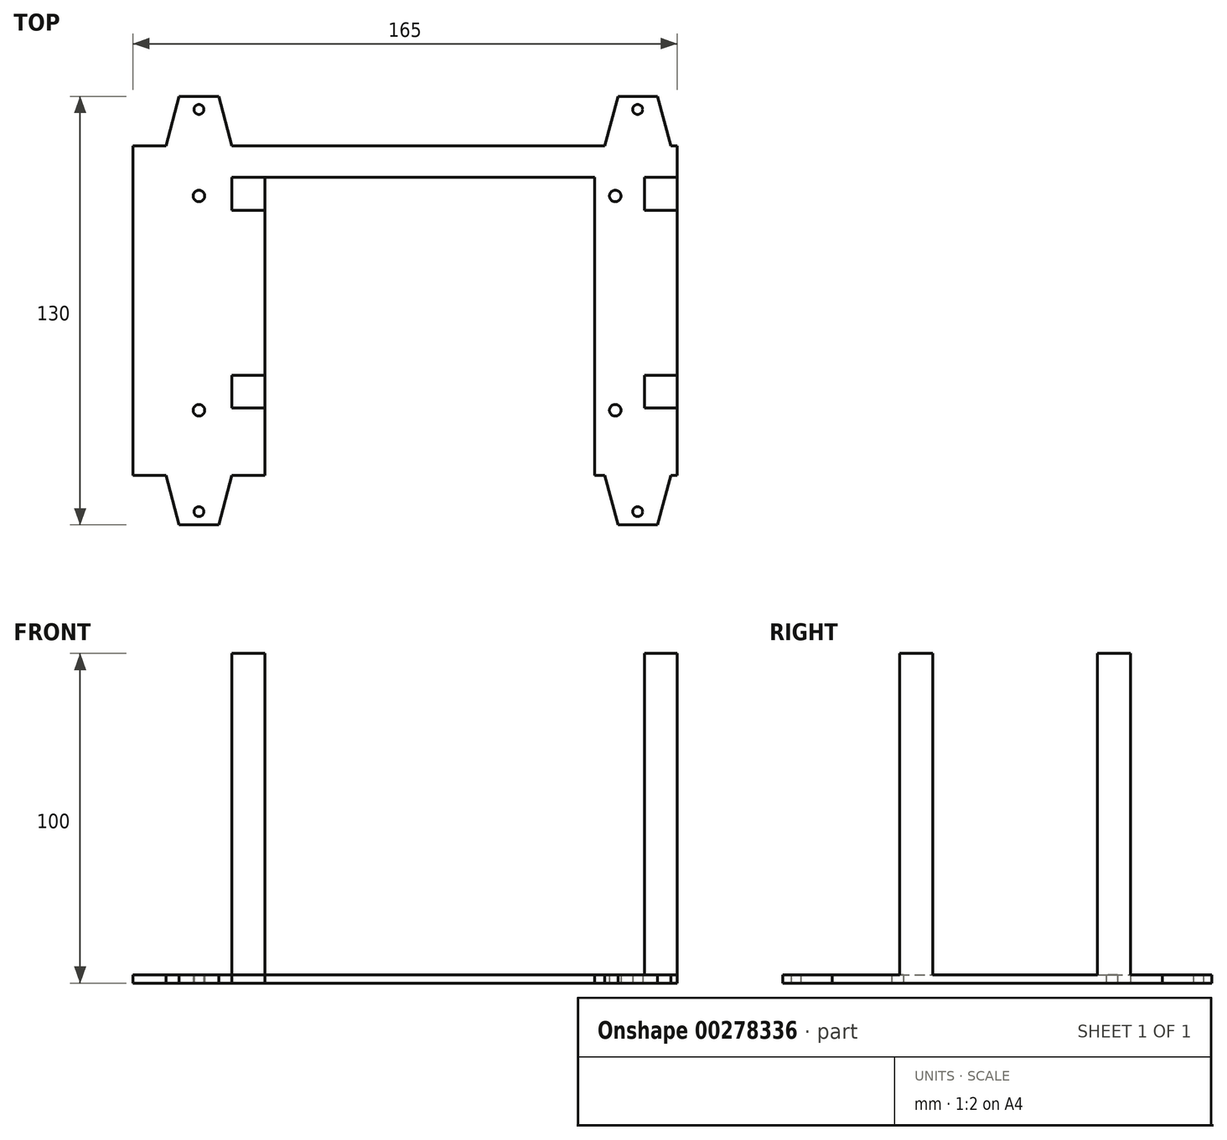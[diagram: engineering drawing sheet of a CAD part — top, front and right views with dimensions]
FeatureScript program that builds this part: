
annotation { "Feature Type Name" : "Feature", "Feature Type Description" : "" }
export const myFeature = defineFeature(function(context is Context, id is Id, definition is map)
    precondition{}
    {
        {
            var Q0;
            Q0=qCreatedBy(makeId("Top.planeOp"),FACE);
            var sketch = newSketch(context, id + "F0", { "sketchPlane" : qUnion([Q0])});
            skLineSegment(sketch, "E0.bottom", {"start": v(-57.92, 32.15) * mm, "end": v(107.08, 32.15) * mm});
            skLineSegment(sketch, "E0.top", {"start": v(-57.92, -67.85) * mm, "end": v(107.08, -67.85) * mm});
            skLineSegment(sketch, "E0.left", {"start": v(-57.92, 32.15) * mm, "end": v(-57.92, -67.85) * mm});
            skLineSegment(sketch, "E0.right", {"start": v(107.08, 32.15) * mm, "end": v(107.08, -67.85) * mm});
            skLineSegment(sketch, "E1.bottom", {"start": v(-17.92, 12.54) * mm, "end": v(82.08, 12.54) * mm});
            skLineSegment(sketch, "E1.top", {"start": v(-17.92, -67.85) * mm, "end": v(82.08, -67.85) * mm});
            skLineSegment(sketch, "E1.left", {"start": v(-17.92, 12.54) * mm, "end": v(-17.92, -67.85) * mm});
            skLineSegment(sketch, "E1.right", {"start": v(82.08, 12.54) * mm, "end": v(82.08, -67.85) * mm});
            skCircle(sketch, "E2", {"center": v(-37.92, 16.9) * mm, "radius": 1.75 * mm});
            skCircle(sketch, "E3.0.1.0", {"center": v(-37.92, -48.1) * mm, "radius": 1.75 * mm});
            skCircle(sketch, "E3.1.0.0", {"center": v(88.28, 16.9) * mm, "radius": 1.75 * mm});
            skCircle(sketch, "E3.1.1.0", {"center": v(88.28, -48.1) * mm, "radius": 1.75 * mm});
            skLineSegment(sketch, "E3.direction1", {"start": v(-37.92, 16.9) * mm, "end": v(88.28, 16.9) * mm, "construction": true});
            skLineSegment(sketch, "E3.direction2", {"start": v(-37.92, 16.9) * mm, "end": v(-37.92, -48.1) * mm, "construction": true});
            skLineSegment(sketch, "E4", {"start": v(-47.92, 32.15) * mm, "end": v(-43.9, 47.15) * mm});
            skLineSegment(sketch, "E5", {"start": v(-43.9, 47.15) * mm, "end": v(-31.94, 47.15) * mm});
            skLineSegment(sketch, "E6", {"start": v(-31.94, 47.15) * mm, "end": v(-27.92, 32.15) * mm});
            skLineSegment(sketch, "E7.MirrorCS", {"start": v(-31.94, -82.85) * mm, "end": v(-27.92, -67.85) * mm});
            skLineSegment(sketch, "E8.MirrorCS", {"start": v(-43.9, -82.85) * mm, "end": v(-31.94, -82.85) * mm});
            skLineSegment(sketch, "E9.MirrorCS", {"start": v(-47.92, -67.85) * mm, "end": v(-43.9, -82.85) * mm});
            skLineSegment(sketch, "E10.1.0.0", {"start": v(89.1, 47.15) * mm, "end": v(101.06, 47.15) * mm});
            skLineSegment(sketch, "E10.1.0.1", {"start": v(85.08, 32.15) * mm, "end": v(89.1, 47.15) * mm});
            skLineSegment(sketch, "E10.1.0.2", {"start": v(101.06, 47.15) * mm, "end": v(105.08, 32.15) * mm});
            skLineSegment(sketch, "E10.1.0.3", {"start": v(85.08, -67.85) * mm, "end": v(89.1, -82.85) * mm});
            skLineSegment(sketch, "E10.1.0.4", {"start": v(101.06, -82.85) * mm, "end": v(105.08, -67.85) * mm});
            skLineSegment(sketch, "E10.1.0.5", {"start": v(89.1, -82.85) * mm, "end": v(101.06, -82.85) * mm});
            skLineSegment(sketch, "E10.direction1", {"start": v(-43.9, -82.85) * mm, "end": v(89.1, -82.85) * mm, "construction": true});
            skCircle(sketch, "E11", {"center": v(-37.92, 43.15) * mm, "radius": 1.5 * mm});
            skCircle(sketch, "E12.0.1.0", {"center": v(-37.92, -78.85) * mm, "radius": 1.5 * mm});
            skCircle(sketch, "E12.1.0.0", {"center": v(95.08, 43.15) * mm, "radius": 1.5 * mm});
            skCircle(sketch, "E12.1.1.0", {"center": v(95.08, -78.85) * mm, "radius": 1.5 * mm});
            skLineSegment(sketch, "E12.direction1", {"start": v(-37.92, 43.15) * mm, "end": v(95.08, 43.15) * mm, "construction": true});
            skLineSegment(sketch, "E12.direction2", {"start": v(-37.92, 43.15) * mm, "end": v(-37.92, -78.85) * mm, "construction": true});
            skLineSegment(sketch, "E13.bottom", {"start": v(-17.92, 12.54) * mm, "end": v(-27.92, 12.54) * mm});
            skLineSegment(sketch, "E13.top", {"start": v(-17.92, 22.54) * mm, "end": v(-27.92, 22.54) * mm});
            skLineSegment(sketch, "E13.left", {"start": v(-17.92, 12.54) * mm, "end": v(-17.92, 22.54) * mm});
            skLineSegment(sketch, "E13.right", {"start": v(-27.92, 12.54) * mm, "end": v(-27.92, 22.54) * mm});
            skLineSegment(sketch, "E14.0.1.0", {"start": v(-17.92, -47.46) * mm, "end": v(-27.92, -47.46) * mm});
            skLineSegment(sketch, "E14.0.1.1", {"start": v(-27.92, -47.46) * mm, "end": v(-27.92, -37.46) * mm});
            skLineSegment(sketch, "E14.0.1.2", {"start": v(-17.92, -37.46) * mm, "end": v(-27.92, -37.46) * mm});
            skLineSegment(sketch, "E14.0.1.3", {"start": v(-17.92, -47.46) * mm, "end": v(-17.92, -37.46) * mm});
            skLineSegment(sketch, "E14.1.0.0", {"start": v(107.08, 12.54) * mm, "end": v(97.08, 12.54) * mm});
            skLineSegment(sketch, "E14.1.0.1", {"start": v(97.08, 12.54) * mm, "end": v(97.08, 22.54) * mm});
            skLineSegment(sketch, "E14.1.0.2", {"start": v(107.08, 22.54) * mm, "end": v(97.08, 22.54) * mm});
            skLineSegment(sketch, "E14.1.0.3", {"start": v(107.08, 12.54) * mm, "end": v(107.08, 22.54) * mm});
            skLineSegment(sketch, "E14.1.1.0", {"start": v(107.08, -47.46) * mm, "end": v(97.08, -47.46) * mm});
            skLineSegment(sketch, "E14.1.1.1", {"start": v(97.08, -47.46) * mm, "end": v(97.08, -37.46) * mm});
            skLineSegment(sketch, "E14.1.1.2", {"start": v(107.08, -37.46) * mm, "end": v(97.08, -37.46) * mm});
            skLineSegment(sketch, "E14.1.1.3", {"start": v(107.08, -47.46) * mm, "end": v(107.08, -37.46) * mm});
            skLineSegment(sketch, "E14.direction1", {"start": v(-27.92, 12.54) * mm, "end": v(97.08, 12.54) * mm, "construction": true});
            skLineSegment(sketch, "E14.direction2", {"start": v(-27.92, 12.54) * mm, "end": v(-27.92, -47.46) * mm, "construction": true});
            skLineSegment(sketch, "E15", {"start": v(-17.92, 22.54) * mm, "end": v(97.08, 22.54) * mm});
            skLineSegment(sketch, "E16", {"start": v(82.08, 12.54) * mm, "end": v(82.08, 22.54) * mm});
            skSolve(sketch);
        }
        {
            var Q0;
            {var subQ6=sQuery(id+"F0.wireOp",EDGE,"E10.1.0.4");Q0=makeQuery(id+"F0.imprint","IMPRINT",FACE,{"disambiguationData":[TD([[makeQuery(id+"F0.imprint","IMPRINT",EDGE,{"derivedFrom":subQ6}),1.0]])]});}
            var Q1;
            {var subQ14=sQuery(id+"F0.wireOp",EDGE,"E0.left");Q1=makeQuery(id+"F0.imprint","IMPRINT",FACE,{"disambiguationData":[TD([[makeQuery(id+"F0.imprint","IMPRINT",EDGE,{"derivedFrom":subQ14}),1.0]])]});}
            var Q2;
            {var subQ1=sQuery(id+"F0.wireOp",EDGE,"E7.MirrorCS");Q2=makeQuery(id+"F0.imprint","IMPRINT",FACE,{"disambiguationData":[TD([[makeQuery(id+"F0.imprint","IMPRINT",EDGE,{"derivedFrom":subQ1}),1.0]])]});}
            var Q3;
            {var subQ1=sQuery(id+"F0.wireOp",EDGE,"E4");Q3=makeQuery(id+"F0.imprint","IMPRINT",FACE,{"disambiguationData":[TD([[makeQuery(id+"F0.imprint","IMPRINT",EDGE,{"derivedFrom":subQ1}),-1.0]])]});}
            var Q4;
            Q4=makeQuery(id+"F0.imprint","IMPRINT",FACE,{"disambiguationData":[TD([[makeQuery(id+"F0.imprint","IMPRINT",EDGE,{"derivedFrom":sQuery(id+"F0.wireOp",EDGE,"E10.1.0.0")}),-1.0]])]});
            var Q5;
            {var subQ1=sQuery(id+"F0.wireOp",EDGE,"E1.right");Q5=makeQuery(id+"F0.imprint","IMPRINT",FACE,{"disambiguationData":[TD([[makeQuery(id+"F0.imprint","IMPRINT",EDGE,{"derivedFrom":subQ1}),1.0]])]});}
            var Q6;
            {var subQ8=sQuery(id+"F0.wireOp",EDGE,"E10.1.0.3");Q6=makeQuery(id+"F0.imprint","IMPRINT",FACE,{"disambiguationData":[TD([[makeQuery(id+"F0.imprint","IMPRINT",EDGE,{"derivedFrom":subQ8}),1.0]])]});}
            extrude(context, id + "F1", {"entities" : qUnion([Q0, Q1, Q2, Q3, Q4, Q5, Q6]), "depth" : 2.5 * mm});
        }
        {
            var Q0;
            Q0=makeQuery(id+"F0.imprint","IMPRINT",FACE,{"disambiguationData":[TD([[makeQuery(id+"F0.imprint","IMPRINT",EDGE,{"derivedFrom":sQuery(id+"F0.wireOp",EDGE,"E13.bottom")}),-1.0]])]});
            var Q1;
            Q1=makeQuery(id+"F0.imprint","IMPRINT",FACE,{"disambiguationData":[TD([[makeQuery(id+"F0.imprint","IMPRINT",EDGE,{"derivedFrom":sQuery(id+"F0.wireOp",EDGE,"E14.1.0.0")}),-1.0]])]});
            var Q2;
            Q2=makeQuery(id+"F0.imprint","IMPRINT",FACE,{"disambiguationData":[TD([[makeQuery(id+"F0.imprint","IMPRINT",EDGE,{"derivedFrom":sQuery(id+"F0.wireOp",EDGE,"E14.1.1.0")}),-1.0]])]});
            var Q3;
            {var subQ0=sQuery(id+"F0.wireOp",EDGE,"E14.1.2.2");Q3=makeQuery(id+"F0.imprint","IMPRINT",FACE,{"disambiguationData":[TD([[makeQuery(id+"F0.imprint","IMPRINT",EDGE,{"derivedFrom":subQ0}),1.0]])]});}
            var Q4;
            Q4=makeQuery(id+"F0.imprint","IMPRINT",FACE,{"disambiguationData":[TD([[makeQuery(id+"F0.imprint","IMPRINT",EDGE,{"derivedFrom":sQuery(id+"F0.wireOp",EDGE,"E14.0.1.0")}),-1.0]])]});
            var Q5;
            {var subQ5=sQuery(id+"F0.wireOp",EDGE,"E14.0.2.2");Q5=makeQuery(id+"F0.imprint","IMPRINT",FACE,{"disambiguationData":[TD([[makeQuery(id+"F0.imprint","IMPRINT",EDGE,{"derivedFrom":subQ5}),1.0]])]});}
            extrude(context, id + "F2", {"entities" : qUnion([Q0, Q1, Q2, Q3, Q4, Q5]), "operationType" : NewBodyOperationType.ADD, "depth" : 100 * mm});
        }
    });
